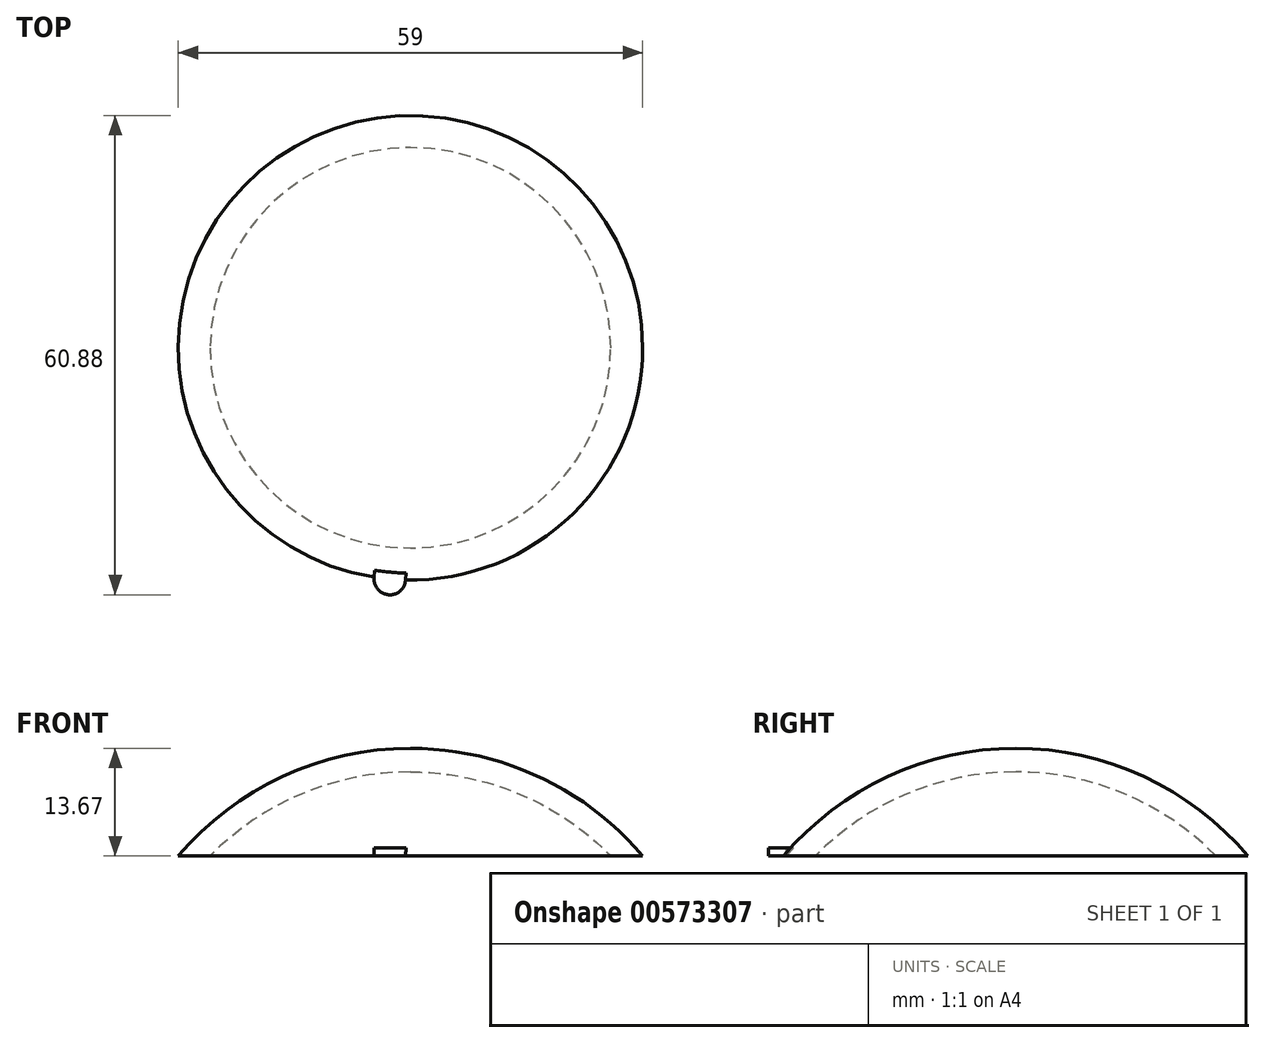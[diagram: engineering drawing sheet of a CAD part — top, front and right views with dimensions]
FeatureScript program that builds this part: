
annotation { "Feature Type Name" : "Feature", "Feature Type Description" : "" }
export const myFeature = defineFeature(function(context is Context, id is Id, definition is map)
    precondition{}
    {
        {
            var Q0;
            Q0=qCreatedBy(makeId("Front.planeOp"),FACE);
            var sketch = newSketch(context, id + "F0", { "sketchPlane" : qUnion([Q0])});
            skArc(sketch, "E0", {"start": v(29.5, 25) * mm, "mid": v(16.26, 35.09) * mm, "end": v(0, 38.67) * mm});
            skLineSegment(sketch, "E1", {"start": v(0, 35.67) * mm, "end": v(0, 38.67) * mm});
            skLineSegment(sketch, "E2", {"start": v(25.44, 25) * mm, "end": v(29.5, 25) * mm});
            skArc(sketch, "E3", {"start": v(25.44, 25) * mm, "mid": v(13.8, 32.9) * mm, "end": v(0, 35.67) * mm});
            skSolve(sketch);
        }
        {
            var Q0;
            Q0=makeQuery(id+"F0.imprint","IMPRINT",FACE,{"disambiguationData":[TD([[makeQuery(id+"F0.imprint","IMPRINT",EDGE,{"derivedFrom":sQuery(id+"F0.wireOp",EDGE,"E0")}),1.0]])]});
            var Q1;
            Q1=sQuery(id+"F0.wireOp",EDGE,"E1");
            revolve(context, id + "F1", {"entities" : qUnion([Q0]), "axis" : qUnion([Q1]), "revolveType" : RevolveType.FULL});
        }
        {
            var Q0;
            Q0=makeQuery(id+"F1.opRevolve","SWEPT_FACE",FACE,{"disambiguationData":[OSD([sQuery(id+"F0.wireOp",EDGE,"E2")])]});
            var sketch = newSketch(context, id + "F2", { "sketchPlane" : qUnion([Q0])});
            skArc(sketch, "E4", {"start": v(-0.63, 29.51) * mm, "mid": v(-2.8, 31.38) * mm, "end": v(-4.6, 29.16) * mm});
            skLineSegment(sketch, "E5", {"start": v(-0.63, 29.51) * mm, "end": v(-0.4, 26.11) * mm});
            skLineSegment(sketch, "E6", {"start": v(-0.4, 26.11) * mm, "end": v(-4.38, 25.86) * mm});
            skLineSegment(sketch, "E7", {"start": v(-4.38, 25.86) * mm, "end": v(-4.6, 29.16) * mm});
            skSolve(sketch);
        }
        {
            var Q0;
            Q0 = qSketchRegion(id + "F2", true);
            extrude(context, id + "F3", {"entities" : qUnion([Q0]), "operationType" : NewBodyOperationType.ADD, "oppositeDirection" : true, "depth" : 1 * mm, "offsetDistance" : 25 * mm});
        }
    });
